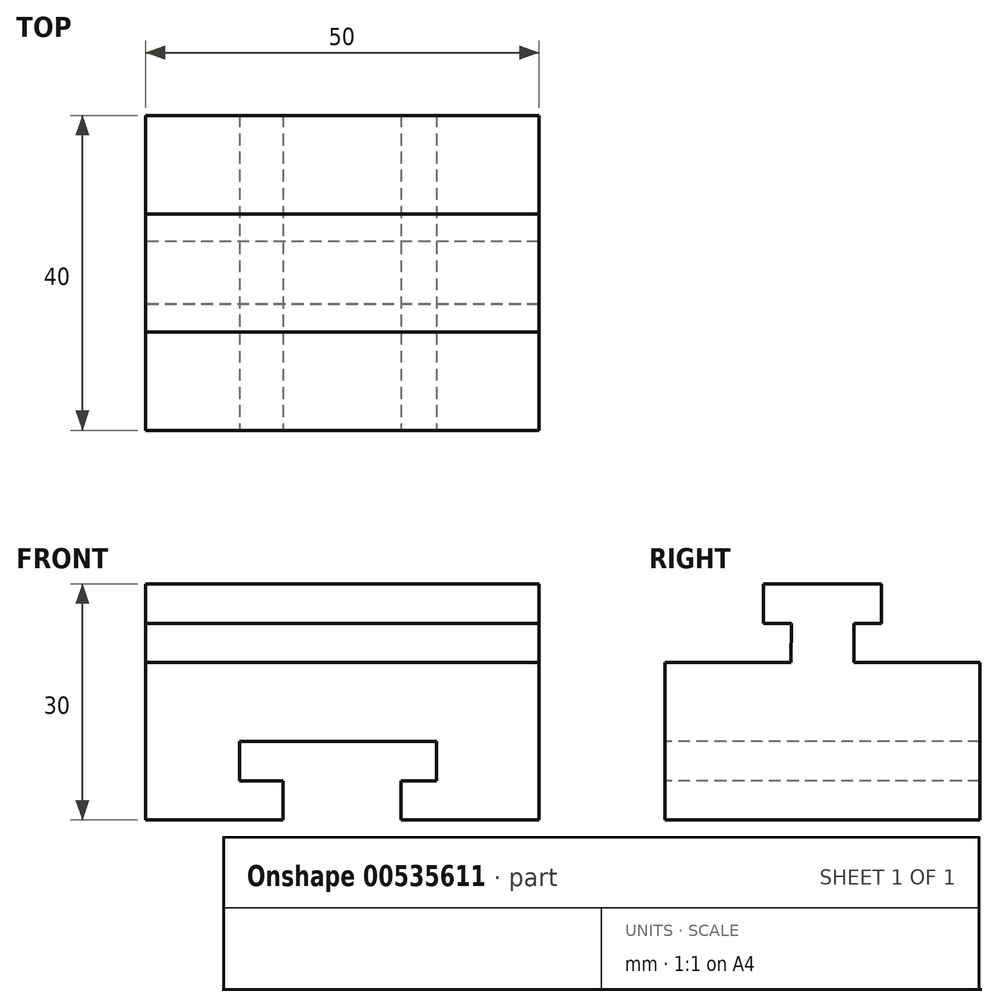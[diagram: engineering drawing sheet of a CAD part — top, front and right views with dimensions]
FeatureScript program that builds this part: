
annotation { "Feature Type Name" : "Feature", "Feature Type Description" : "" }
export const myFeature = defineFeature(function(context is Context, id is Id, definition is map)
    precondition{}
    {
        {
            var Q0;
            Q0=qCreatedBy(makeId("Front.planeOp"),FACE);
            var sketch = newSketch(context, id + "F0", { "sketchPlane" : qUnion([Q0])});
            skLineSegment(sketch, "E0.bottom", {"start": v(25, -15) * mm, "end": v(-25, -15) * mm});
            skLineSegment(sketch, "E0.top", {"start": v(25, 15) * mm, "end": v(-25, 15) * mm});
            skLineSegment(sketch, "E0.left", {"start": v(25, -15) * mm, "end": v(25, 15) * mm});
            skLineSegment(sketch, "E0.right", {"start": v(-25, -15) * mm, "end": v(-25, 15) * mm});
            skPoint(sketch, "E0.middle", {"position": v(0, 0) * mm});
            skSolve(sketch);
        }
        {
            var Q0;
            Q0 = qSketchRegion(id + "F0", true);
            extrude(context, id + "F1", {"entities" : qUnion([Q0]), "depth" : 40 * mm, "offsetDistance" : 25 * mm});
        }
        {
            var Q0;
            Q0=makeQuery(id+"F1.opExtrude","SWEPT_FACE",FACE,{"disambiguationData":[OSD([sQuery(id+"F0.wireOp",EDGE,"E0.right")])]});
            var sketch = newSketch(context, id + "F2", { "sketchPlane" : qUnion([Q0])});
            skLineSegment(sketch, "E1", {"start": v(0, -15) * mm, "end": v(12.5, -15) * mm, "construction": true});
            skLineSegment(sketch, "E2", {"start": v(40, -15) * mm, "end": v(27.5, -15) * mm, "construction": true});
            skLineSegment(sketch, "E3", {"start": v(12.5, -15) * mm, "end": v(27.5, -15) * mm, "construction": true});
            skLineSegment(sketch, "E4", {"start": v(16, 10) * mm, "end": v(12.5, 10) * mm});
            skLineSegment(sketch, "E5", {"start": v(12.5, 10) * mm, "end": v(12.5, 15) * mm});
            skLineSegment(sketch, "E6", {"start": v(27.5, 15) * mm, "end": v(27.5, 10) * mm});
            skLineSegment(sketch, "E7", {"start": v(27.5, 10) * mm, "end": v(23.94, 10) * mm});
            skLineSegment(sketch, "E8", {"start": v(23.94, 10) * mm, "end": v(24, 5) * mm});
            skLineSegment(sketch, "E9", {"start": v(40, 5) * mm, "end": v(24, 5) * mm});
            skLineSegment(sketch, "E10", {"start": v(16, 5) * mm, "end": v(16, 10) * mm});
            skLineSegment(sketch, "E11", {"start": v(12.5, 15) * mm, "end": v(27.5, 15) * mm});
            skLineSegment(sketch, "E12", {"start": v(16, 5) * mm, "end": v(0, 5) * mm});
            skLineSegment(sketch, "E13", {"start": v(0, 5) * mm, "end": v(0, 15) * mm});
            skLineSegment(sketch, "E14", {"start": v(0, 15) * mm, "end": v(12.5, 15) * mm});
            skLineSegment(sketch, "E15", {"start": v(27.5, 15) * mm, "end": v(40, 15) * mm});
            skLineSegment(sketch, "E16", {"start": v(40, 15) * mm, "end": v(40, 5) * mm});
            skSolve(sketch);
        }
        {
            var Q0;
            Q0=makeQuery(id+"F2.imprint","IMPRINT",FACE,{"disambiguationData":[TD([[makeQuery(id+"F2.imprint","IMPRINT",EDGE,{"derivedFrom":sQuery(id+"F2.wireOp",EDGE,"E4")}),1.0]])]});
            var Q1;
            Q1=makeQuery(id+"F2.imprint","IMPRINT",FACE,{"disambiguationData":[TD([[makeQuery(id+"F2.imprint","IMPRINT",EDGE,{"derivedFrom":sQuery(id+"F2.wireOp",EDGE,"E6")}),1.0]])]});
            extrude(context, id + "F3", {"entities" : qUnion([Q0, Q1]), "operationType" : NewBodyOperationType.REMOVE, "endBound" : BoundingType.THROUGH_ALL, "oppositeDirection" : true, "depth" : 25 * mm, "offsetDistance" : 25 * mm});
        }
        {
            var Q0;
            Q0=makeQuery(id+"F1.opExtrude","CAP_FACE",FACE,{"disambiguationData":[OSD([sQuery(id+"F0.wireOp",EDGE,"E0.bottom"),sQuery(id+"F0.wireOp",EDGE,"E0.top"),sQuery(id+"F0.wireOp",EDGE,"E0.left"),sQuery(id+"F0.wireOp",EDGE,"E0.right")])],"isStart":false});
            var sketch = newSketch(context, id + "F4", { "sketchPlane" : qUnion([Q0])});
            skLineSegment(sketch, "E17", {"start": v(-25, -15) * mm, "end": v(-7.5, -15) * mm, "construction": true});
            skLineSegment(sketch, "E18", {"start": v(25, -15) * mm, "end": v(7.5, -15) * mm, "construction": true});
            skLineSegment(sketch, "E19", {"start": v(-7.5, -15) * mm, "end": v(-7.5, -10) * mm});
            skLineSegment(sketch, "E20", {"start": v(-7.5, -10) * mm, "end": v(-13.03, -10) * mm});
            skLineSegment(sketch, "E21", {"start": v(-13.03, -10) * mm, "end": v(-13.03, -5) * mm});
            skLineSegment(sketch, "E22", {"start": v(-13.03, -5) * mm, "end": v(11.97, -5) * mm});
            skLineSegment(sketch, "E23", {"start": v(11.97, -5) * mm, "end": v(11.97, -10) * mm});
            skLineSegment(sketch, "E24", {"start": v(11.97, -10) * mm, "end": v(7.5, -10) * mm});
            skLineSegment(sketch, "E25", {"start": v(7.5, -10) * mm, "end": v(7.5, -15) * mm});
            skSolve(sketch);
        }
        {
            var Q0;
            Q0 = qSketchRegion(id + "F4", true);
            var Q1;
            {var subQ0=sQuery(id+"F4.wireOp",EDGE,"E19");Q1=makeQuery(id+"F4.imprint","IMPRINT",FACE,{"disambiguationData":[TD([[makeQuery(id+"F4.imprint","IMPRINT",EDGE,{"derivedFrom":subQ0}),-1.0]])]});}
            extrude(context, id + "F5", {"entities" : qUnion([Q0, Q1]), "operationType" : NewBodyOperationType.REMOVE, "endBound" : BoundingType.THROUGH_ALL, "oppositeDirection" : true, "depth" : 25 * mm, "offsetDistance" : 25 * mm});
        }
    });
